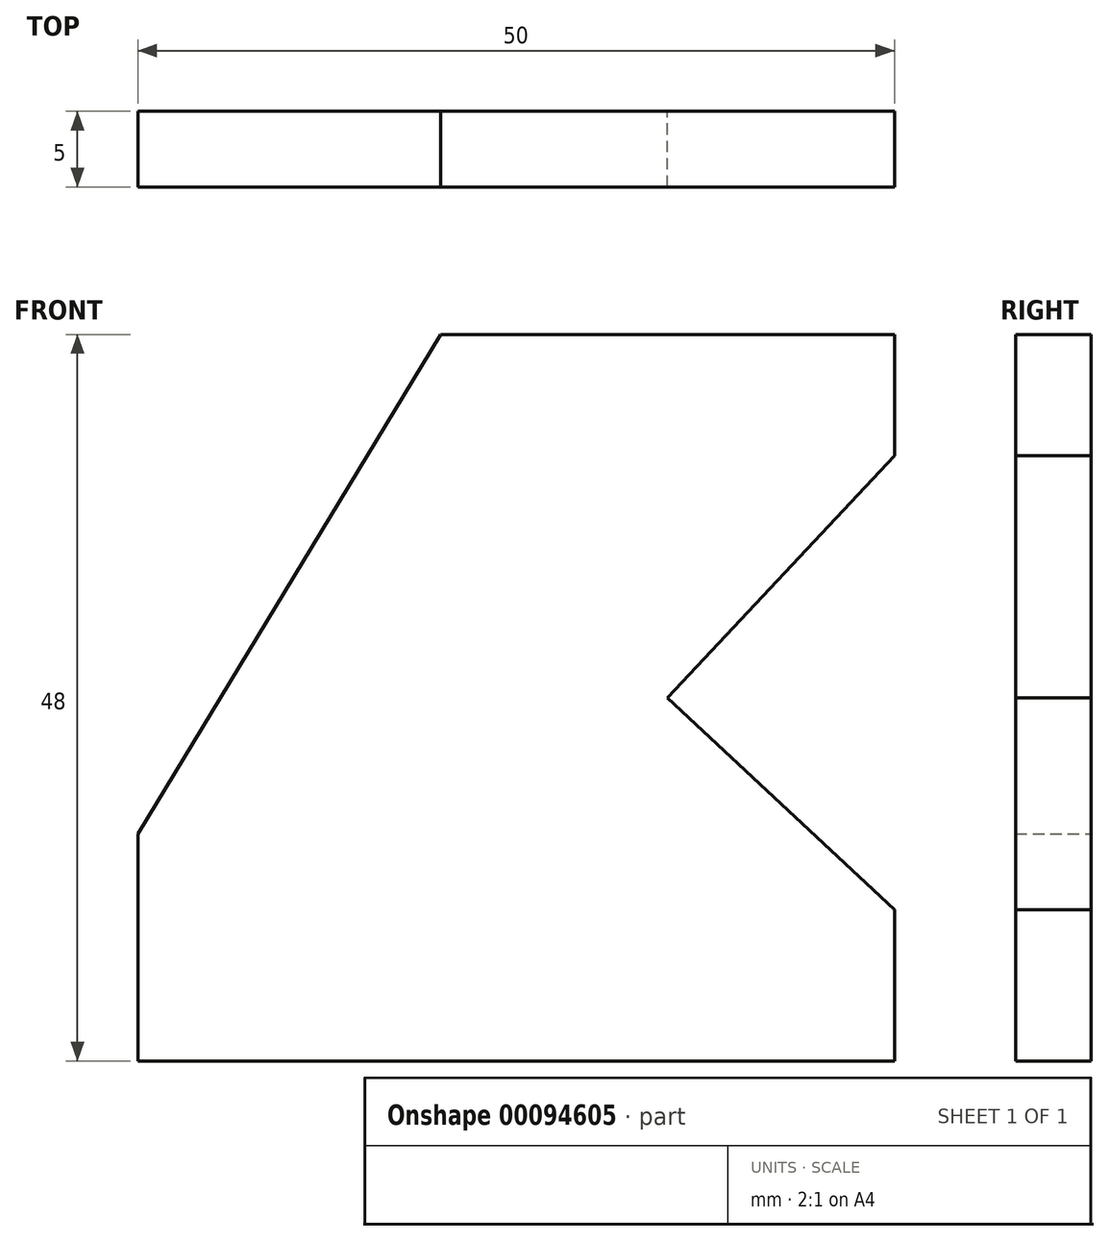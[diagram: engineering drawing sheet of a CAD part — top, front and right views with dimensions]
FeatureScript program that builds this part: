
annotation { "Feature Type Name" : "Feature", "Feature Type Description" : "" }
export const myFeature = defineFeature(function(context is Context, id is Id, definition is map)
    precondition{}
    {
        {
            var Q0;
            Q0=qCreatedBy(makeId("Front.planeOp"),FACE);
            var sketch = newSketch(context, id + "F0", { "sketchPlane" : qUnion([Q0])});
            skLineSegment(sketch, "E0", {"start": v(0, 24) * mm, "end": v(0, -24) * mm, "construction": true});
            skLineSegment(sketch, "E1", {"start": v(0, -24) * mm, "end": v(0, -14) * mm});
            skLineSegment(sketch, "E2", {"start": v(0, 24) * mm, "end": v(0, 16) * mm});
            skLineSegment(sketch, "E3", {"start": v(0, 0) * mm, "end": v(-15, 0) * mm, "construction": true});
            skLineSegment(sketch, "E4", {"start": v(0, 16) * mm, "end": v(-15, 0) * mm});
            skLineSegment(sketch, "E5", {"start": v(-15, 0) * mm, "end": v(0, -14) * mm});
            skLineSegment(sketch, "E6", {"start": v(0, -24) * mm, "end": v(-50, -24) * mm});
            skLineSegment(sketch, "E7", {"start": v(-50, -24) * mm, "end": v(-50, -9) * mm});
            skLineSegment(sketch, "E8", {"start": v(0, 24) * mm, "end": v(-30, 24) * mm});
            skLineSegment(sketch, "E9", {"start": v(-30, 24) * mm, "end": v(-50, -9) * mm});
            skSolve(sketch);
        }
        {
            var Q0;
            Q0=makeQuery(id+"F0.imprint","IMPRINT",FACE,{"disambiguationData":[TD([[makeQuery(id+"F0.imprint","IMPRINT",EDGE,{"derivedFrom":sQuery(id+"F0.wireOp",EDGE,"E1")}),1.0]])]});
            extrude(context, id + "F1", {"entities" : qUnion([Q0]), "depth" : 5 * mm});
        }
    });
